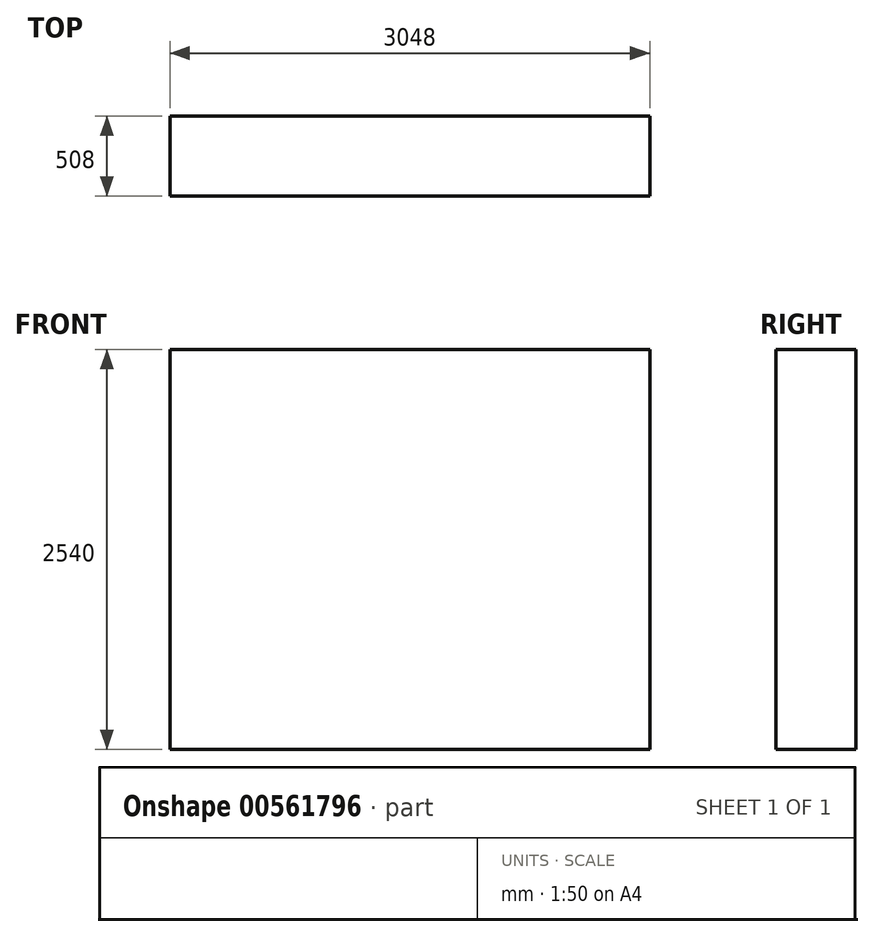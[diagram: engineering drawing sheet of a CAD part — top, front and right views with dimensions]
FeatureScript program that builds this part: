
annotation { "Feature Type Name" : "Feature", "Feature Type Description" : "" }
export const myFeature = defineFeature(function(context is Context, id is Id, definition is map)
    precondition{}
    {
        {
            var Q0;
            Q0=qCreatedBy(makeId("Front.planeOp"),FACE);
            var sketch = newSketch(context, id + "F0", { "sketchPlane" : qUnion([Q0])});
            skLineSegment(sketch, "E0.bottom", {"start": v(0, 0) * mm, "end": v(3048, 0) * mm});
            skLineSegment(sketch, "E0.top", {"start": v(0, 2540) * mm, "end": v(3048, 2540) * mm});
            skLineSegment(sketch, "E0.left", {"start": v(0, 0) * mm, "end": v(0, 2540) * mm});
            skLineSegment(sketch, "E0.right", {"start": v(3048, 0) * mm, "end": v(3048, 2540) * mm});
            skSolve(sketch);
        }
        {
            var Q0;
            Q0 = qSketchRegion(id + "F0", true);
            extrude(context, id + "F1", {"entities" : qUnion([Q0]), "depth" : 508 * mm, "offsetDistance" : 25.4 * mm});
        }
    });
